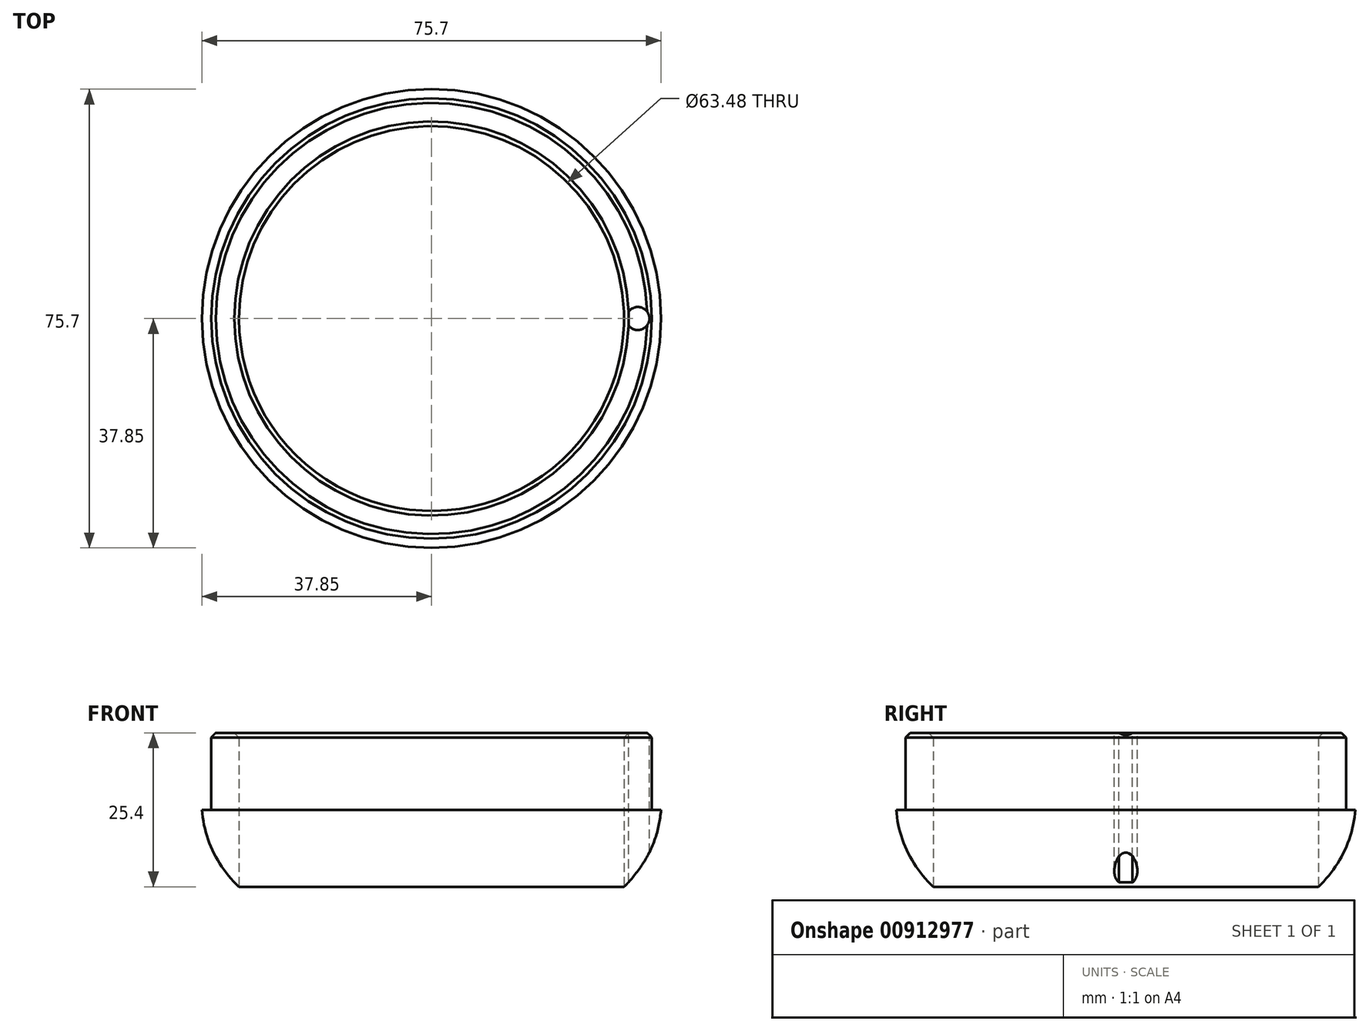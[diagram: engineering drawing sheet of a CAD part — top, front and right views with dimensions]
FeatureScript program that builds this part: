
annotation { "Feature Type Name" : "Feature", "Feature Type Description" : "" }
export const myFeature = defineFeature(function(context is Context, id is Id, definition is map)
    precondition{}
    {
        {
            var Q0;
            Q0=qCreatedBy(makeId("Front.planeOp"),FACE);
            var sketch = newSketch(context, id + "F0", { "sketchPlane" : qUnion([Q0])});
            skLineSegment(sketch, "E0", {"start": v(0, 0) * mm, "end": v(0, 15.74) * mm});
            skLineSegment(sketch, "E1", {"start": v(0, 0) * mm, "end": v(31.74, 0) * mm});
            skLineSegment(sketch, "E2", {"start": v(31.74, 0) * mm, "end": v(31.74, 25.4) * mm});
            skLineSegment(sketch, "E3", {"start": v(31.74, 25.4) * mm, "end": v(36.32, 25.4) * mm});
            skLineSegment(sketch, "E4", {"start": v(37.85, 12.7) * mm, "end": v(36.32, 12.7) * mm});
            skLineSegment(sketch, "E5", {"start": v(36.32, 12.7) * mm, "end": v(36.32, 25.4) * mm});
            skPoint(sketch, "E6.orphan", {"position": v(34.6, 25.4) * mm});
            skPoint(sketch, "E7.start.orphan", {"position": v(18.57, 0) * mm});
            skArc(sketch, "E8", {"start": v(31.74, 0) * mm, "mid": v(36, 5.77) * mm, "end": v(37.85, 12.7) * mm});
            skLineSegment(sketch, "E9", {"start": v(37.85, 12.7) * mm, "end": v(37.85, 18.7) * mm});
            skSolve(sketch);
        }
        {
            var Q0;
            Q0=makeQuery(id+"F0.imprint","IMPRINT",FACE,{"disambiguationData":[TD([[makeQuery(id+"F0.imprint","IMPRINT",EDGE,{"derivedFrom":sQuery(id+"F0.wireOp",EDGE,"E2")}),-1.0]])]});
            var Q1;
            Q1=sQuery(id+"F0.wireOp",EDGE,"E0");
            revolve(context, id + "F1", {"surfaceOperationType" : NewSurfaceOperationType.NEW, "entities" : qUnion([Q0]), "axis" : qUnion([Q1]), "revolveType" : RevolveType.FULL});
        }
        {
            var Q0;
            Q0=makeQuery(id+"F1.opRevolve","SWEPT_EDGE",EDGE,{"disambiguationData":[OSD([sQuery(id+"F0.wireOp",EDGE,"E2"),sQuery(id+"F0.wireOp",EDGE,"E3")])]});
            var Q1;
            Q1=makeQuery(id+"F1.opRevolve","SWEPT_EDGE",EDGE,{"disambiguationData":[OSD([sQuery(id+"F0.wireOp",EDGE,"E3"),sQuery(id+"F0.wireOp",EDGE,"E5")])]});
            chamfer(context, id + "F2", {"entities" : qUnion([Q0, Q1]), "width" : 0.76 * mm, "tangentPropagation" : true});
        }
        {
            var Q0;
            Q0=makeQuery(id+"F1.opRevolve","SWEPT_FACE",FACE,{"disambiguationData":[OSD([sQuery(id+"F0.wireOp",EDGE,"E3")])]});
            var sketch = newSketch(context, id + "F3", { "sketchPlane" : qUnion([Q0])});
            skLineSegment(sketch, "E10", {"start": v(0, 0) * mm, "end": v(31.74, 0) * mm});
            skCircle(sketch, "E11", {"center": v(34.03, 0) * mm, "radius": 1.9 * mm});
            skLineSegment(sketch, "E12", {"start": v(31.74, 0) * mm, "end": v(34.03, 0) * mm});
            skSolve(sketch);
        }
        {
            var Q0;
            Q0=makeQuery(id+"F3.imprint","IMPRINT",FACE,{"disambiguationData":[TD([[makeQuery(id+"F3.imprint","IMPRINT",EDGE,{"derivedFrom":sQuery(id+"F3.wireOp",EDGE,"E11")}),1.0]])]});
            var Q1;
            {var subQ0=sQuery(id+"F3.wireOp",EDGE,"E11");var subQ1=sQuery(id+"F0.wireOp",EDGE,"E3");var subQ2=makeQuery(id+"F2.opChamfer","BLEND_EDGE",EDGE,{"blendedFrom":[makeQuery(id+"F1.opRevolve","SWEPT_EDGE",EDGE,{"disambiguationData":[OSD([subQ1,sQuery(id+"F0.wireOp",EDGE,"E5")])]}),makeQuery(id+"F1.opRevolve","SWEPT_FACE",FACE,{"disambiguationData":[OSD([subQ1])]})],"blendedInto":[makeQuery(id+"F1.opRevolve","SWEPT_FACE",FACE,{"disambiguationData":[OSD([subQ1])]})]});var subQ3=makeQuery(id+"F3.imprint","INTERSECT",VERTEX,{"disambiguationData":[OD(0.0)],"derivedFrom":[subQ2,subQ0]});Q1=makeQuery(id+"F3.imprint","IMPRINT",FACE,{"disambiguationData":[TD([[makeQuery(id+"F3.imprint","IMPRINT",EDGE,{"disambiguationData":[TD([[subQ3,1.0]])],"derivedFrom":subQ0}),1.0]])]});}
            extrude(context, id + "F4", {"entities" : qUnion([Q0, Q1]), "operationType" : NewBodyOperationType.REMOVE, "oppositeDirection" : true, "depth" : 25.4 * mm, "offsetDistance" : 25.4 * mm});
        }
    });
